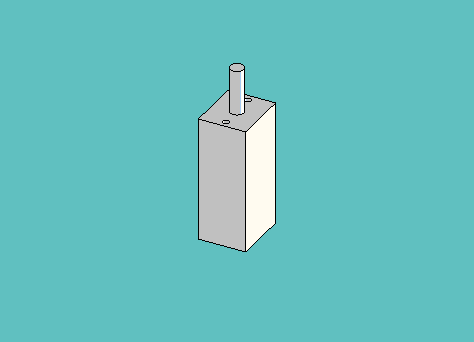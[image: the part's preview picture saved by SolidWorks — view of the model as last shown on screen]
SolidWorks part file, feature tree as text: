
SOLIDWORKS PART (.sldprt)
format: sldprt  version: not decoded by parser v0  size: 173,056 bytes
history: native  units: mm
features: sketch x3, extrude x2, material x1, cut_extrude x1 (+11 scaffold rows collapsed)
feature tree (18):
  scaffold x11  (default folders/planes/origin — collapsed)
  material  "Material <not specified>"
  sketch  "Sketch1"  dims[D1=11.9888mm D2=10.1092mm]
  extrude  "Extrude1"  Depth=26.3144mm
  sketch  "Sketch2"  dims[D1=3.0mm]
  extrude  "Extrude2"  Depth=9.525mm
  sketch  "Sketch3"  dims[D1=8.9916mm D2=1.3208mm D3=1.3208mm]
  cut_extrude  "Cut-Extrude1"  Depth=3.175mm
decode coverage: 6 of 6 modeling features carry decoded parameters
note: suppression state not decoded; provenance and decode notes live in map.json
